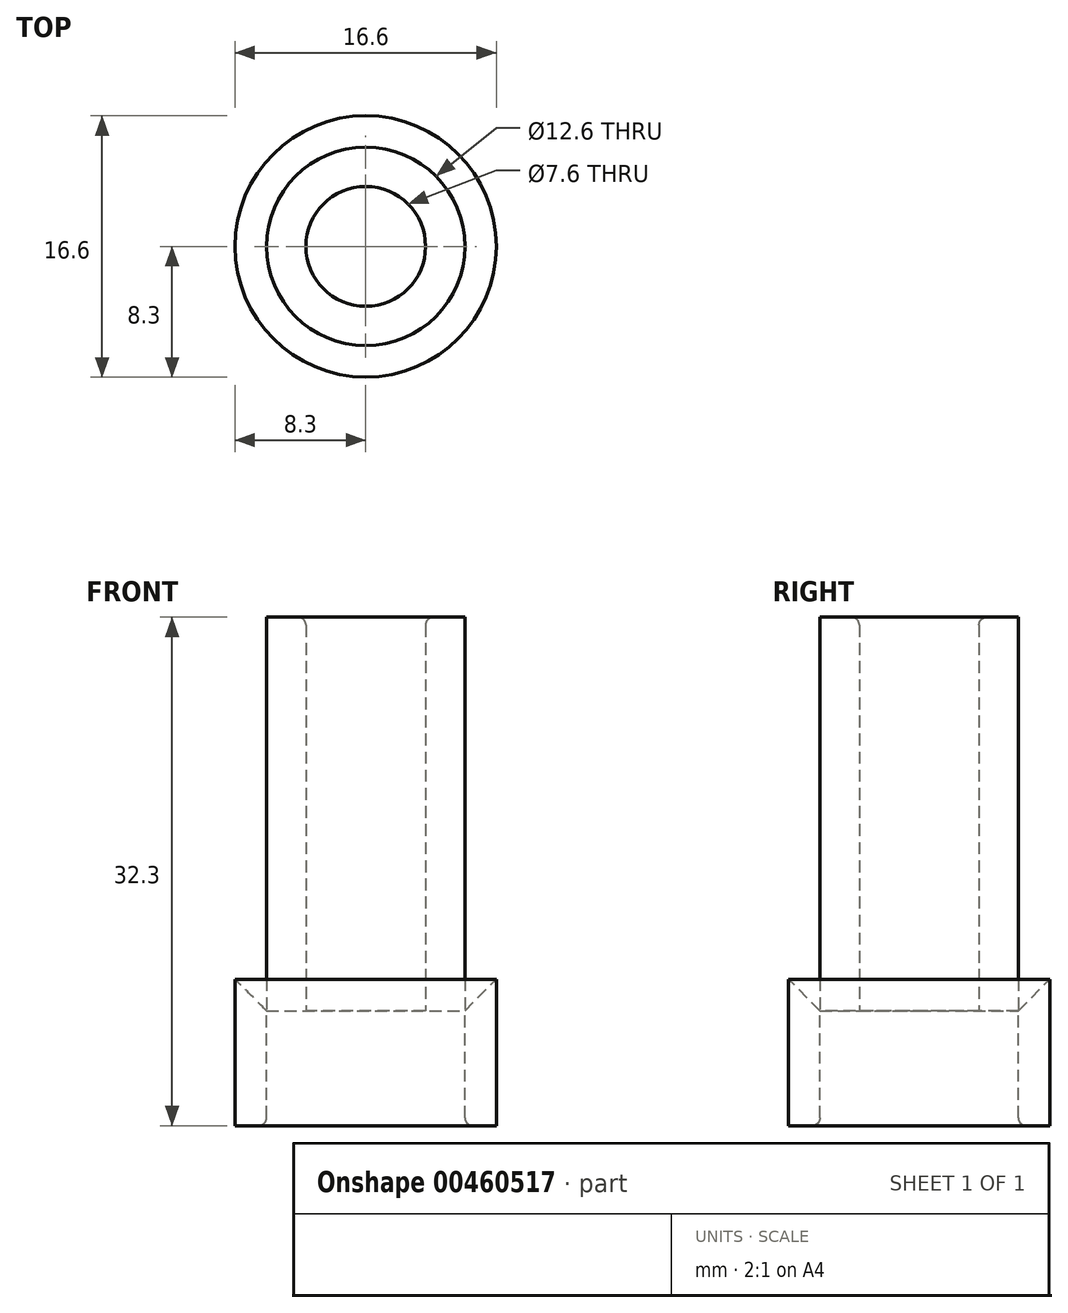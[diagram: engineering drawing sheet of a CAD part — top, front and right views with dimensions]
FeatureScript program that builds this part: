
annotation { "Feature Type Name" : "Feature", "Feature Type Description" : "" }
export const myFeature = defineFeature(function(context is Context, id is Id, definition is map)
    precondition{}
    {
        {
            var Q0;
            Q0=qCreatedBy(makeId("Top.planeOp"),FACE);
            var sketch = newSketch(context, id + "F0", { "sketchPlane" : qUnion([Q0])});
            skCircle(sketch, "E0", {"center": v(0, 0) * mm, "radius": 6.3 * mm});
            skCircle(sketch, "E1", {"center": v(0, 0) * mm, "radius": 3.8 * mm});
            skSolve(sketch);
        }
        {
            var Q0;
            Q0=qSketchRegion(id+"F0",true);
            extrude(context, id + "F1", {"entities" : qUnion([Q0]), "depth" : 25 * mm, "offsetDistance" : 25 * mm});
        }
        {
            var Q0;
            Q0=makeQuery(id+"F1.opExtrude","CAP_FACE",FACE,{"disambiguationData":[OSD([sQuery(id+"F0.wireOp",EDGE,"E0"),sQuery(id+"F0.wireOp",EDGE,"E1")])],"isStart":true});
            var sketch = newSketch(context, id + "F2", { "sketchPlane" : qUnion([Q0])});
            skCircle(sketch, "E2", {"center": v(0, 0) * mm, "radius": 8.3 * mm});
            skCircle(sketch, "E3", {"center": v(0, 0) * mm, "radius": 6.3 * mm});
            skSolve(sketch);
        }
        {
            var Q0;
            Q0=makeQuery(id+"F2.imprint","IMPRINT",FACE,{"disambiguationData":[TD([[makeQuery(id+"F2.imprint","IMPRINT",EDGE,{"derivedFrom":sQuery(id+"F2.wireOp",EDGE,"E2")}),1.0]])]});
            var Q1;
            Q1=makeQuery(id+"F2.imprint","IMPRINT",FACE,{"disambiguationData":[TD([[makeQuery(id+"F2.imprint","IMPRINT",EDGE,{"derivedFrom":sQuery(id+"F2.wireOp",EDGE,"E3")}),1.0]])]});
            extrude(context, id + "F3", {"entities" : qUnion([Q0, Q1]), "depth" : 7.3 * mm, "hasSecondDirection" : true, "secondDirectionOppositeDirection" : true, "secondDirectionDepth" : 2 * mm});
        }
        {
            var Q0;
            Q0=makeQuery(id+"F3.opExtrude","CAP_EDGE",EDGE,{"disambiguationData":[OSD([sQuery(id+"F2.wireOp",EDGE,"E3")])],"isStart":true});
            chamfer(context, id + "F4", {"entities" : qUnion([Q0]), "width" : 2 * mm, "tangentPropagation" : true});
        }
        {
            var Q0;
            Q0=makeQuery(id+"F1.opExtrude","CAP_EDGE",EDGE,{"disambiguationData":[OSD([sQuery(id+"F0.wireOp",EDGE,"E1")])],"isStart":false});
            var Q1;
            Q1=makeQuery(id+"F3.opExtrude","CAP_EDGE",EDGE,{"disambiguationData":[OSD([sQuery(id+"F2.wireOp",EDGE,"E3")])],"isStart":false});
            fillet(context, id + "F5", {"entities" : qUnion([Q0, Q1]), "radius" : 0.5 * mm, "tangentPropagation" : true, "allowEdgeOverflow" : false});
        }
    });
